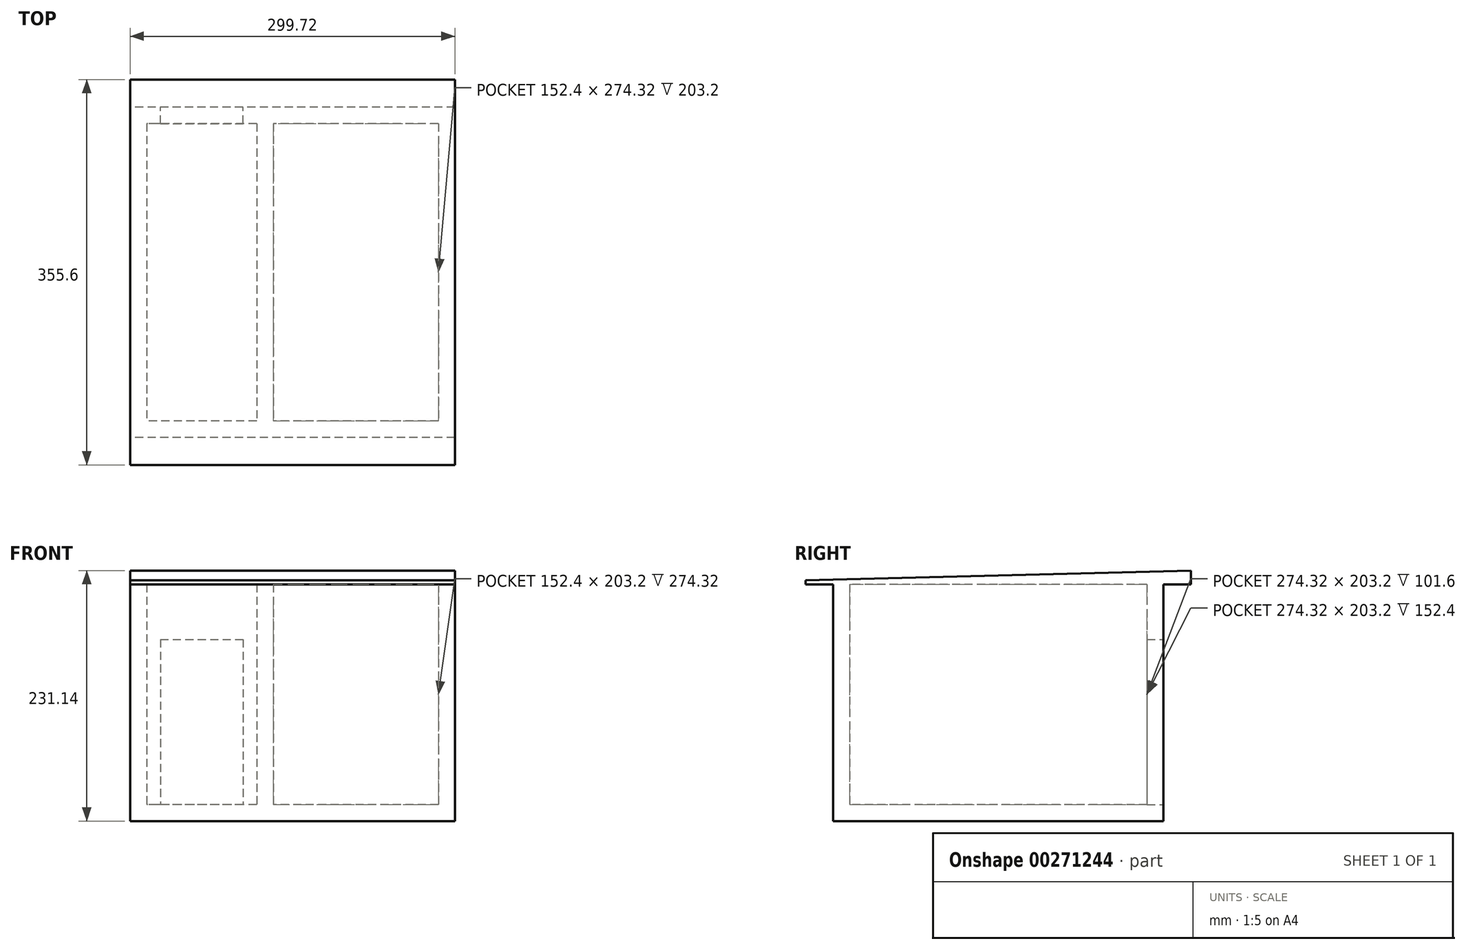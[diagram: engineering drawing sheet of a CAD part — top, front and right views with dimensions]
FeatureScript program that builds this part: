
annotation { "Feature Type Name" : "Feature", "Feature Type Description" : "" }
export const myFeature = defineFeature(function(context is Context, id is Id, definition is map)
    precondition{}
    {
        {
            var Q0;
            Q0=qCreatedBy(makeId("Top.planeOp"),FACE);
            var sketch = newSketch(context, id + "F0", { "sketchPlane" : qUnion([Q0])});
            skLineSegment(sketch, "E0.bottom", {"start": v(149.86, 152.4) * mm, "end": v(-149.86, 152.4) * mm});
            skLineSegment(sketch, "E0.top", {"start": v(149.86, -152.4) * mm, "end": v(-149.86, -152.4) * mm});
            skLineSegment(sketch, "E0.left", {"start": v(149.86, 152.4) * mm, "end": v(149.86, -152.4) * mm});
            skLineSegment(sketch, "E0.right", {"start": v(-149.86, 152.4) * mm, "end": v(-149.86, -152.4) * mm});
            skPoint(sketch, "E0.middle", {"position": v(0, 0) * mm});
            skLineSegment(sketch, "E1.bottom", {"start": v(134.62, 137.16) * mm, "end": v(-134.62, 137.16) * mm});
            skLineSegment(sketch, "E1.top", {"start": v(134.62, -137.16) * mm, "end": v(-134.62, -137.16) * mm});
            skLineSegment(sketch, "E1.left", {"start": v(134.62, 137.16) * mm, "end": v(134.62, -137.16) * mm});
            skLineSegment(sketch, "E1.right", {"start": v(-134.62, 137.16) * mm, "end": v(-134.62, -137.16) * mm});
            skLineSegment(sketch, "E2", {"start": v(-17.78, 152.4) * mm, "end": v(-17.78, -152.4) * mm});
            skLineSegment(sketch, "E3", {"start": v(-33.02, 152.4) * mm, "end": v(-33.02, -152.4) * mm});
            skSolve(sketch);
        }
        {
            var Q0;
            {var subQ4=sQuery(id+"F0.wireOp",EDGE,"E0.right");Q0=makeQuery(id+"F0.imprint","IMPRINT",FACE,{"disambiguationData":[TD([[makeQuery(id+"F0.imprint","IMPRINT",EDGE,{"derivedFrom":subQ4}),1.0]])]});}
            var Q1;
            {var subQ0=sQuery(id+"F0.wireOp",EDGE,"E2");var subQ1=sQuery(id+"F0.wireOp",EDGE,"E0.bottom");var subQ2=makeQuery(id+"F0.imprint","INTERSECT",VERTEX,{"derivedFrom":[subQ1,subQ0]});Q1=makeQuery(id+"F0.imprint","IMPRINT",FACE,{"disambiguationData":[TD([[makeQuery(id+"F0.imprint","IMPRINT",EDGE,{"disambiguationData":[TD([[subQ2,-1.0]])],"derivedFrom":subQ1}),1.0]])]});}
            var Q2;
            {var subQ0=sQuery(id+"F0.wireOp",EDGE,"E2");var subQ1=sQuery(id+"F0.wireOp",EDGE,"E0.top");var subQ2=makeQuery(id+"F0.imprint","INTERSECT",VERTEX,{"derivedFrom":[subQ1,subQ0]});Q2=makeQuery(id+"F0.imprint","IMPRINT",FACE,{"disambiguationData":[TD([[makeQuery(id+"F0.imprint","IMPRINT",EDGE,{"disambiguationData":[TD([[subQ2,-1.0]])],"derivedFrom":subQ1}),-1.0]])]});}
            var Q3;
            {var subQ0=sQuery(id+"F0.wireOp",EDGE,"E2");var subQ1=sQuery(id+"F0.wireOp",EDGE,"E1.bottom");var subQ2=makeQuery(id+"F0.imprint","INTERSECT",VERTEX,{"derivedFrom":[subQ1,subQ0]});Q3=makeQuery(id+"F0.imprint","IMPRINT",FACE,{"disambiguationData":[TD([[makeQuery(id+"F0.imprint","IMPRINT",EDGE,{"disambiguationData":[TD([[subQ2,-1.0]])],"derivedFrom":subQ1}),1.0]])]});}
            var Q4;
            {var subQ4=sQuery(id+"F0.wireOp",EDGE,"E0.left");Q4=makeQuery(id+"F0.imprint","IMPRINT",FACE,{"disambiguationData":[TD([[makeQuery(id+"F0.imprint","IMPRINT",EDGE,{"derivedFrom":subQ4}),-1.0]])]});}
            extrude(context, id + "F1", {"entities" : qUnion([Q0, Q1, Q2, Q3, Q4]), "depth" : 203.2 * mm});
        }
        {
            var Q0;
            Q0=makeQuery(id+"F1.opExtrude","CAP_FACE",FACE,{"disambiguationData":[OSD([sQuery(id+"F0.wireOp",EDGE,"E0.bottom"),sQuery(id+"F0.wireOp",EDGE,"E0.top"),sQuery(id+"F0.wireOp",EDGE,"E0.left"),sQuery(id+"F0.wireOp",EDGE,"E0.right"),sQuery(id+"F0.wireOp",EDGE,"E1.bottom"),sQuery(id+"F0.wireOp",EDGE,"E1.top"),sQuery(id+"F0.wireOp",EDGE,"E1.left"),sQuery(id+"F0.wireOp",EDGE,"E1.right"),sQuery(id+"F0.wireOp",EDGE,"E2"),sQuery(id+"F0.wireOp",EDGE,"E3")])],"isStart":true});
            var sketch = newSketch(context, id + "F2", { "sketchPlane" : qUnion([Q0])});
            skLineSegment(sketch, "E4.bottom", {"start": v(149.86, 152.4) * mm, "end": v(-149.86, 152.4) * mm});
            skLineSegment(sketch, "E4.top", {"start": v(149.86, -152.4) * mm, "end": v(-149.86, -152.4) * mm});
            skLineSegment(sketch, "E4.left", {"start": v(149.86, 152.4) * mm, "end": v(149.86, -152.4) * mm});
            skLineSegment(sketch, "E4.right", {"start": v(-149.86, 152.4) * mm, "end": v(-149.86, -152.4) * mm});
            skPoint(sketch, "E4.middle", {"position": v(0, 0) * mm});
            skSolve(sketch);
        }
        {
            var Q0;
            Q0 = qSketchRegion(id + "F2", true);
            extrude(context, id + "F3", {"entities" : qUnion([Q0]), "operationType" : NewBodyOperationType.ADD, "depth" : 15.24 * mm});
        }
        {
            var Q0;
            Q0=makeQuery(id+"F1.opExtrude","CAP_FACE",FACE,{"disambiguationData":[OSD([sQuery(id+"F0.wireOp",EDGE,"E0.bottom"),sQuery(id+"F0.wireOp",EDGE,"E0.top"),sQuery(id+"F0.wireOp",EDGE,"E0.left"),sQuery(id+"F0.wireOp",EDGE,"E0.right"),sQuery(id+"F0.wireOp",EDGE,"E1.bottom"),sQuery(id+"F0.wireOp",EDGE,"E1.top"),sQuery(id+"F0.wireOp",EDGE,"E1.left"),sQuery(id+"F0.wireOp",EDGE,"E1.right"),sQuery(id+"F0.wireOp",EDGE,"E2"),sQuery(id+"F0.wireOp",EDGE,"E3")])],"isStart":false});
            var sketch = newSketch(context, id + "F4", { "sketchPlane" : qUnion([Q0])});
            skLineSegment(sketch, "E5.bottom", {"start": v(149.86, 177.8) * mm, "end": v(-149.86, 177.8) * mm});
            skLineSegment(sketch, "E5.top", {"start": v(149.86, -177.8) * mm, "end": v(-149.86, -177.8) * mm});
            skLineSegment(sketch, "E5.left", {"start": v(149.86, 177.8) * mm, "end": v(149.86, -177.8) * mm});
            skLineSegment(sketch, "E5.right", {"start": v(-149.86, 177.8) * mm, "end": v(-149.86, -177.8) * mm});
            skPoint(sketch, "E5.middle", {"position": v(0, 0) * mm});
            skSolve(sketch);
        }
        {
            var Q0;
            Q0 = qSketchRegion(id + "F4", true);
            extrude(context, id + "F5", {"entities" : qUnion([Q0]), "operationType" : NewBodyOperationType.ADD, "depth" : 12.7 * mm});
        }
        {
            var Q0;
            Q0=makeQuery(id+"F3.boolean.opBoolean","MERGE",FACE,{"derivedFrom":[makeQuery(id+"F1.opExtrude","SWEPT_FACE",FACE,{"disambiguationData":[OSD([sQuery(id+"F0.wireOp",EDGE,"E0.bottom")])]}),makeQuery(id+"F3.opExtrude","SWEPT_FACE",FACE,{"disambiguationData":[OSD([sQuery(id+"F2.wireOp",EDGE,"E4.top")])]})]});
            var sketch = newSketch(context, id + "F6", { "sketchPlane" : qUnion([Q0])});
            skLineSegment(sketch, "E6.bottom", {"start": v(45.72, 0) * mm, "end": v(121.92, 0) * mm});
            skLineSegment(sketch, "E6.top", {"start": v(45.72, 152.4) * mm, "end": v(121.92, 152.4) * mm});
            skLineSegment(sketch, "E6.left", {"start": v(45.72, 0) * mm, "end": v(45.72, 152.4) * mm});
            skLineSegment(sketch, "E6.right", {"start": v(121.92, 0) * mm, "end": v(121.92, 152.4) * mm});
            skSolve(sketch);
        }
        {
            var Q0;
            Q0=makeQuery(id+"F6.imprint","IMPRINT",FACE,{"disambiguationData":[TD([[makeQuery(id+"F6.imprint","IMPRINT",EDGE,{"derivedFrom":sQuery(id+"F6.wireOp",EDGE,"E6.bottom")}),1.0]])]});
            extrude(context, id + "F7", {"entities" : qUnion([Q0]), "operationType" : NewBodyOperationType.REMOVE, "oppositeDirection" : true, "depth" : 25.4 * mm});
        }
        {
            var Q0;
            Q0=makeQuery(id+"F5.opExtrude","SWEPT_FACE",FACE,{"disambiguationData":[OSD([sQuery(id+"F4.wireOp",EDGE,"E5.left")])]});
            var sketch = newSketch(context, id + "F8", { "sketchPlane" : qUnion([Q0])});
            skLineSegment(sketch, "E7.bottom", {"start": v(177.8, 215.9) * mm, "end": v(-177.8, 215.9) * mm});
            skLineSegment(sketch, "E7.top", {"start": v(177.8, 203.2) * mm, "end": v(-177.8, 203.2) * mm});
            skLineSegment(sketch, "E7.left", {"start": v(177.8, 215.9) * mm, "end": v(177.8, 203.2) * mm});
            skLineSegment(sketch, "E7.right", {"start": v(-177.8, 215.9) * mm, "end": v(-177.8, 203.2) * mm});
            skPoint(sketch, "E8", {"position": v(-177.8, 207.01) * mm});
            skLineSegment(sketch, "E9", {"start": v(-177.8, 207.01) * mm, "end": v(177.8, 215.9) * mm});
            skSolve(sketch);
        }
        {
            var Q0;
            {var subQ0=sQuery(id+"F8.wireOp",EDGE,"E7.bottom");Q0=makeQuery(id+"F8.imprint","IMPRINT",FACE,{"disambiguationData":[TD([[makeQuery(id+"F8.imprint","IMPRINT",EDGE,{"derivedFrom":subQ0}),1.0]])]});}
            extrude(context, id + "F9", {"entities" : qUnion([Q0]), "operationType" : NewBodyOperationType.REMOVE, "oppositeDirection" : true, "depth" : 373.13 * mm});
        }
    });
